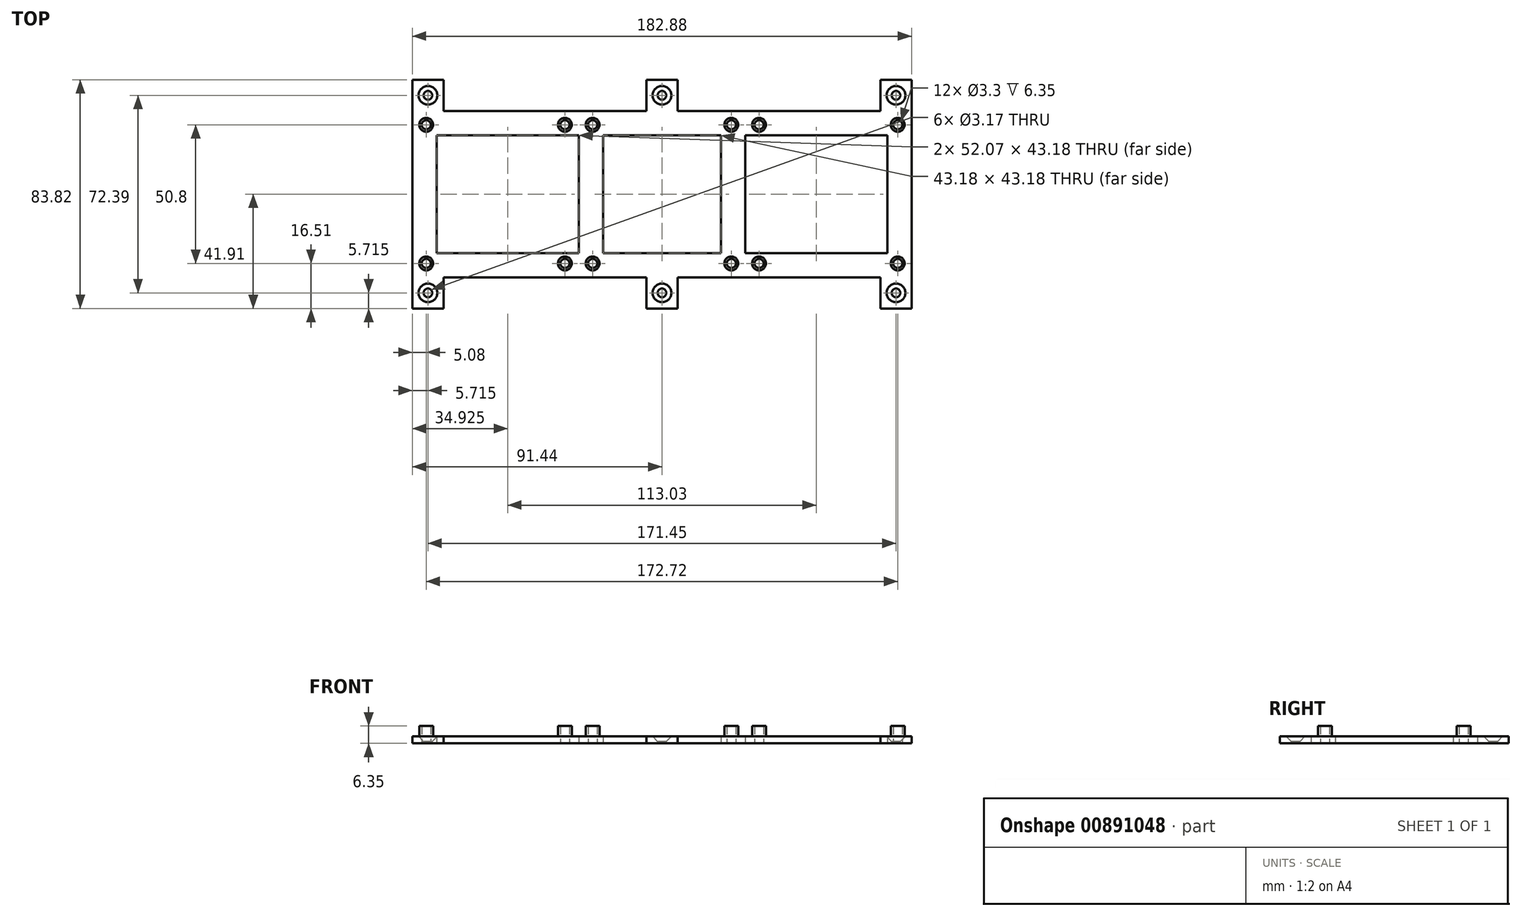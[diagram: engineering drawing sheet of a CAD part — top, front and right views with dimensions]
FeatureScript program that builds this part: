
annotation { "Feature Type Name" : "Feature", "Feature Type Description" : "" }
export const myFeature = defineFeature(function(context is Context, id is Id, definition is map)
    precondition{}
    {
        {
            var Q0;
            Q0=qCreatedBy(makeId("Top.planeOp"),FACE);
            var sketch = newSketch(context, id + "F0", { "sketchPlane" : qUnion([Q0])});
            skLineSegment(sketch, "E0.bottom", {"start": v(30.48, 30.48) * mm, "end": v(-30.48, 30.48) * mm});
            skLineSegment(sketch, "E0.top", {"start": v(30.48, -30.48) * mm, "end": v(-30.48, -30.48) * mm});
            skLineSegment(sketch, "E0.left", {"start": v(30.48, 30.48) * mm, "end": v(30.48, -30.48) * mm});
            skLineSegment(sketch, "E0.right", {"start": v(-30.48, 30.48) * mm, "end": v(-30.48, -30.48) * mm});
            skPoint(sketch, "E0.middle", {"position": v(0, 0) * mm});
            skCircle(sketch, "E1", {"center": v(-25.4, 25.4) * mm, "radius": 2.54 * mm});
            skCircle(sketch, "E2", {"center": v(25.4, 25.4) * mm, "radius": 2.54 * mm});
            skCircle(sketch, "E3", {"center": v(25.4, -25.4) * mm, "radius": 2.54 * mm});
            skCircle(sketch, "E4", {"center": v(-25.4, -25.4) * mm, "radius": 2.54 * mm});
            skLineSegment(sketch, "E5.bottom", {"start": v(21.59, 21.6) * mm, "end": v(-21.59, 21.6) * mm});
            skLineSegment(sketch, "E5.top", {"start": v(21.59, -21.6) * mm, "end": v(-21.59, -21.6) * mm});
            skLineSegment(sketch, "E5.left", {"start": v(21.59, 21.6) * mm, "end": v(21.59, -21.6) * mm});
            skLineSegment(sketch, "E5.right", {"start": v(-21.59, 21.6) * mm, "end": v(-21.59, -21.6) * mm});
            skLineSegment(sketch, "E6.bottom", {"start": v(-30.48, 30.48) * mm, "end": v(-91.44, 30.48) * mm});
            skLineSegment(sketch, "E6.top", {"start": v(-30.48, 21.6) * mm, "end": v(-91.44, 21.6) * mm});
            skLineSegment(sketch, "E6.left", {"start": v(-30.48, 30.48) * mm, "end": v(-30.48, 21.6) * mm});
            skLineSegment(sketch, "E6.right", {"start": v(-91.44, 30.48) * mm, "end": v(-91.44, 21.59) * mm});
            skLineSegment(sketch, "E7.bottom", {"start": v(-30.48, -30.48) * mm, "end": v(-91.44, -30.48) * mm});
            skLineSegment(sketch, "E7.top", {"start": v(-30.48, -21.6) * mm, "end": v(-91.44, -21.6) * mm});
            skLineSegment(sketch, "E7.left", {"start": v(-30.48, -30.48) * mm, "end": v(-30.48, -21.6) * mm});
            skLineSegment(sketch, "E7.right", {"start": v(-91.44, -30.48) * mm, "end": v(-91.44, -21.6) * mm});
            skLineSegment(sketch, "E8.bottom", {"start": v(-91.44, 21.6) * mm, "end": v(-82.55, 21.6) * mm});
            skLineSegment(sketch, "E8.top", {"start": v(-91.44, -21.6) * mm, "end": v(-82.55, -21.6) * mm});
            skLineSegment(sketch, "E8.left", {"start": v(-91.44, 21.59) * mm, "end": v(-91.44, -21.6) * mm});
            skLineSegment(sketch, "E8.right", {"start": v(-82.55, 21.59) * mm, "end": v(-82.55, -21.6) * mm});
            skLineSegment(sketch, "E9.bottom", {"start": v(30.48, 30.48) * mm, "end": v(91.44, 30.48) * mm});
            skLineSegment(sketch, "E9.top", {"start": v(30.48, 21.6) * mm, "end": v(91.44, 21.6) * mm});
            skLineSegment(sketch, "E9.left", {"start": v(30.48, 30.48) * mm, "end": v(30.48, 21.6) * mm});
            skLineSegment(sketch, "E9.right", {"start": v(91.44, 30.48) * mm, "end": v(91.44, 21.6) * mm});
            skLineSegment(sketch, "E10.bottom", {"start": v(30.48, -30.48) * mm, "end": v(91.44, -30.48) * mm});
            skLineSegment(sketch, "E10.top", {"start": v(30.48, -21.6) * mm, "end": v(91.44, -21.6) * mm});
            skLineSegment(sketch, "E10.left", {"start": v(30.48, -30.48) * mm, "end": v(30.48, -21.6) * mm});
            skLineSegment(sketch, "E10.right", {"start": v(91.44, -30.48) * mm, "end": v(91.44, -21.6) * mm});
            skLineSegment(sketch, "E11.bottom", {"start": v(91.44, 21.6) * mm, "end": v(82.55, 21.6) * mm});
            skLineSegment(sketch, "E11.top", {"start": v(91.44, -21.6) * mm, "end": v(82.55, -21.6) * mm});
            skLineSegment(sketch, "E11.left", {"start": v(91.44, 21.6) * mm, "end": v(91.44, -21.6) * mm});
            skLineSegment(sketch, "E11.right", {"start": v(82.55, 21.6) * mm, "end": v(82.55, -21.6) * mm});
            skCircle(sketch, "E12", {"center": v(35.56, 25.4) * mm, "radius": 2.54 * mm});
            skCircle(sketch, "E13", {"center": v(86.36, 25.4) * mm, "radius": 2.54 * mm});
            skCircle(sketch, "E14", {"center": v(86.36, -25.4) * mm, "radius": 2.54 * mm});
            skCircle(sketch, "E15", {"center": v(35.56, -25.4) * mm, "radius": 2.54 * mm});
            skCircle(sketch, "E16", {"center": v(-35.56, 25.4) * mm, "radius": 2.54 * mm});
            skCircle(sketch, "E17", {"center": v(-86.36, 25.4) * mm, "radius": 2.54 * mm});
            skCircle(sketch, "E18", {"center": v(-86.36, -25.4) * mm, "radius": 2.54 * mm});
            skCircle(sketch, "E19", {"center": v(-35.56, -25.4) * mm, "radius": 2.54 * mm});
            skLineSegment(sketch, "E20.bottom", {"start": v(-91.44, 30.48) * mm, "end": v(-80.01, 30.48) * mm});
            skLineSegment(sketch, "E20.top", {"start": v(-91.44, 41.91) * mm, "end": v(-80.01, 41.91) * mm});
            skLineSegment(sketch, "E20.left", {"start": v(-91.44, 30.48) * mm, "end": v(-91.44, 41.91) * mm});
            skLineSegment(sketch, "E20.right", {"start": v(-80.01, 30.48) * mm, "end": v(-80.01, 41.91) * mm});
            skLineSegment(sketch, "E21.bottom", {"start": v(-91.44, -30.48) * mm, "end": v(-80.01, -30.48) * mm});
            skLineSegment(sketch, "E21.top", {"start": v(-91.44, -41.91) * mm, "end": v(-80.01, -41.91) * mm});
            skLineSegment(sketch, "E21.left", {"start": v(-91.44, -30.48) * mm, "end": v(-91.44, -41.91) * mm});
            skLineSegment(sketch, "E21.right", {"start": v(-80.01, -30.48) * mm, "end": v(-80.01, -41.91) * mm});
            skLineSegment(sketch, "E22.bottom", {"start": v(91.44, -30.48) * mm, "end": v(80.01, -30.48) * mm});
            skLineSegment(sketch, "E22.top", {"start": v(91.44, -41.91) * mm, "end": v(80.01, -41.91) * mm});
            skLineSegment(sketch, "E22.left", {"start": v(91.44, -30.48) * mm, "end": v(91.44, -41.91) * mm});
            skLineSegment(sketch, "E22.right", {"start": v(80.01, -30.48) * mm, "end": v(80.01, -41.91) * mm});
            skLineSegment(sketch, "E23.bottom", {"start": v(91.44, 30.48) * mm, "end": v(80.01, 30.48) * mm});
            skLineSegment(sketch, "E23.top", {"start": v(91.44, 41.91) * mm, "end": v(80.01, 41.91) * mm});
            skLineSegment(sketch, "E23.left", {"start": v(91.44, 30.48) * mm, "end": v(91.44, 41.91) * mm});
            skLineSegment(sketch, "E23.right", {"start": v(80.01, 30.48) * mm, "end": v(80.01, 41.91) * mm});
            skLineSegment(sketch, "E24.bottom", {"start": v(-5.72, 30.48) * mm, "end": v(5.71, 30.48) * mm});
            skLineSegment(sketch, "E24.top", {"start": v(-5.72, 41.91) * mm, "end": v(5.71, 41.91) * mm});
            skLineSegment(sketch, "E24.left", {"start": v(-5.72, 30.48) * mm, "end": v(-5.72, 41.91) * mm});
            skLineSegment(sketch, "E24.right", {"start": v(5.71, 30.48) * mm, "end": v(5.71, 41.91) * mm});
            skPoint(sketch, "E25.firstSnap0", {"position": v(-5.72, 36.2) * mm});
            skLineSegment(sketch, "E25.bottom", {"start": v(-5.72, -30.48) * mm, "end": v(5.71, -30.48) * mm});
            skLineSegment(sketch, "E25.top", {"start": v(-5.72, -41.91) * mm, "end": v(5.71, -41.91) * mm});
            skLineSegment(sketch, "E25.left", {"start": v(-5.72, -30.48) * mm, "end": v(-5.72, -41.91) * mm});
            skLineSegment(sketch, "E25.right", {"start": v(5.71, -30.48) * mm, "end": v(5.71, -41.91) * mm});
            skSolve(sketch);
        }
        {
            var Q0;
            Q0=makeQuery(id+"F0.imprint","IMPRINT",FACE,{"disambiguationData":[TD([[makeQuery(id+"F0.imprint","IMPRINT",EDGE,{"derivedFrom":sQuery(id+"F0.wireOp",EDGE,"E1")}),-1.0]])]});
            var Q1;
            {var subQ4=sQuery(id+"F0.wireOp",EDGE,"E6.right");Q1=makeQuery(id+"F0.imprint","IMPRINT",FACE,{"disambiguationData":[TD([[makeQuery(id+"F0.imprint","IMPRINT",EDGE,{"derivedFrom":subQ4}),1.0]])]});}
            var Q2;
            {var subQ0=sQuery(id+"F0.wireOp",EDGE,"E8.left");Q2=makeQuery(id+"F0.imprint","IMPRINT",FACE,{"disambiguationData":[TD([[makeQuery(id+"F0.imprint","IMPRINT",EDGE,{"derivedFrom":subQ0}),1.0]])]});}
            var Q3;
            {var subQ7=sQuery(id+"F0.wireOp",EDGE,"E7.right");Q3=makeQuery(id+"F0.imprint","IMPRINT",FACE,{"disambiguationData":[TD([[makeQuery(id+"F0.imprint","IMPRINT",EDGE,{"derivedFrom":subQ7}),-1.0]])]});}
            var Q4;
            {var subQ4=sQuery(id+"F0.wireOp",EDGE,"E9.right");Q4=makeQuery(id+"F0.imprint","IMPRINT",FACE,{"disambiguationData":[TD([[makeQuery(id+"F0.imprint","IMPRINT",EDGE,{"derivedFrom":subQ4}),-1.0]])]});}
            var Q5;
            {var subQ7=sQuery(id+"F0.wireOp",EDGE,"E10.right");Q5=makeQuery(id+"F0.imprint","IMPRINT",FACE,{"disambiguationData":[TD([[makeQuery(id+"F0.imprint","IMPRINT",EDGE,{"derivedFrom":subQ7}),1.0]])]});}
            var Q6;
            {var subQ0=sQuery(id+"F0.wireOp",EDGE,"E11.left");Q6=makeQuery(id+"F0.imprint","IMPRINT",FACE,{"disambiguationData":[TD([[makeQuery(id+"F0.imprint","IMPRINT",EDGE,{"derivedFrom":subQ0}),-1.0]])]});}
            var Q7;
            Q7=makeQuery(id+"F0.imprint","IMPRINT",FACE,{"disambiguationData":[TD([[makeQuery(id+"F0.imprint","IMPRINT",EDGE,{"derivedFrom":sQuery(id+"F0.wireOp",EDGE,"E20.top")}),-1.0]])]});
            var Q8;
            Q8=makeQuery(id+"F0.imprint","IMPRINT",FACE,{"disambiguationData":[TD([[makeQuery(id+"F0.imprint","IMPRINT",EDGE,{"derivedFrom":sQuery(id+"F0.wireOp",EDGE,"E23.top")}),1.0]])]});
            var Q9;
            Q9=makeQuery(id+"F0.imprint","IMPRINT",FACE,{"disambiguationData":[TD([[makeQuery(id+"F0.imprint","IMPRINT",EDGE,{"derivedFrom":sQuery(id+"F0.wireOp",EDGE,"E22.top")}),-1.0]])]});
            var Q10;
            Q10=makeQuery(id+"F0.imprint","IMPRINT",FACE,{"disambiguationData":[TD([[makeQuery(id+"F0.imprint","IMPRINT",EDGE,{"derivedFrom":sQuery(id+"F0.wireOp",EDGE,"E21.top")}),1.0]])]});
            var Q11;
            Q11=makeQuery(id+"F0.imprint","IMPRINT",FACE,{"disambiguationData":[TD([[makeQuery(id+"F0.imprint","IMPRINT",EDGE,{"derivedFrom":sQuery(id+"F0.wireOp",EDGE,"E24.top")}),-1.0]])]});
            var Q12;
            Q12=makeQuery(id+"F0.imprint","IMPRINT",FACE,{"disambiguationData":[TD([[makeQuery(id+"F0.imprint","IMPRINT",EDGE,{"derivedFrom":sQuery(id+"F0.wireOp",EDGE,"E25.top")}),1.0]])]});
            extrude(context, id + "F1", {"entities" : qUnion([Q0, Q1, Q2, Q3, Q4, Q5, Q6, Q7, Q8, Q9, Q10, Q11, Q12]), "depth" : 2.54 * mm, "offsetDistance" : 25.4 * mm});
        }
        {
            var Q0;
            Q0=makeQuery(id+"F0.imprint","IMPRINT",FACE,{"disambiguationData":[TD([[makeQuery(id+"F0.imprint","IMPRINT",EDGE,{"derivedFrom":sQuery(id+"F0.wireOp",EDGE,"E1")}),1.0]])]});
            var Q1;
            Q1=makeQuery(id+"F0.imprint","IMPRINT",FACE,{"disambiguationData":[TD([[makeQuery(id+"F0.imprint","IMPRINT",EDGE,{"derivedFrom":sQuery(id+"F0.wireOp",EDGE,"E2")}),1.0]])]});
            var Q2;
            Q2=makeQuery(id+"F0.imprint","IMPRINT",FACE,{"disambiguationData":[TD([[makeQuery(id+"F0.imprint","IMPRINT",EDGE,{"derivedFrom":sQuery(id+"F0.wireOp",EDGE,"E3")}),1.0]])]});
            var Q3;
            Q3=makeQuery(id+"F0.imprint","IMPRINT",FACE,{"disambiguationData":[TD([[makeQuery(id+"F0.imprint","IMPRINT",EDGE,{"derivedFrom":sQuery(id+"F0.wireOp",EDGE,"E4")}),1.0]])]});
            var Q4;
            Q4=makeQuery(id+"F0.imprint","IMPRINT",FACE,{"disambiguationData":[TD([[makeQuery(id+"F0.imprint","IMPRINT",EDGE,{"derivedFrom":sQuery(id+"F0.wireOp",EDGE,"E17")}),1.0]])]});
            var Q5;
            Q5=makeQuery(id+"F0.imprint","IMPRINT",FACE,{"disambiguationData":[TD([[makeQuery(id+"F0.imprint","IMPRINT",EDGE,{"derivedFrom":sQuery(id+"F0.wireOp",EDGE,"E18")}),1.0]])]});
            var Q6;
            Q6=makeQuery(id+"F0.imprint","IMPRINT",FACE,{"disambiguationData":[TD([[makeQuery(id+"F0.imprint","IMPRINT",EDGE,{"derivedFrom":sQuery(id+"F0.wireOp",EDGE,"E16")}),1.0]])]});
            var Q7;
            Q7=makeQuery(id+"F0.imprint","IMPRINT",FACE,{"disambiguationData":[TD([[makeQuery(id+"F0.imprint","IMPRINT",EDGE,{"derivedFrom":sQuery(id+"F0.wireOp",EDGE,"E19")}),1.0]])]});
            var Q8;
            Q8=makeQuery(id+"F0.imprint","IMPRINT",FACE,{"disambiguationData":[TD([[makeQuery(id+"F0.imprint","IMPRINT",EDGE,{"derivedFrom":sQuery(id+"F0.wireOp",EDGE,"E15")}),1.0]])]});
            var Q9;
            Q9=makeQuery(id+"F0.imprint","IMPRINT",FACE,{"disambiguationData":[TD([[makeQuery(id+"F0.imprint","IMPRINT",EDGE,{"derivedFrom":sQuery(id+"F0.wireOp",EDGE,"E14")}),1.0]])]});
            var Q10;
            Q10=makeQuery(id+"F0.imprint","IMPRINT",FACE,{"disambiguationData":[TD([[makeQuery(id+"F0.imprint","IMPRINT",EDGE,{"derivedFrom":sQuery(id+"F0.wireOp",EDGE,"E13")}),1.0]])]});
            var Q11;
            Q11=makeQuery(id+"F0.imprint","IMPRINT",FACE,{"disambiguationData":[TD([[makeQuery(id+"F0.imprint","IMPRINT",EDGE,{"derivedFrom":sQuery(id+"F0.wireOp",EDGE,"E12")}),1.0]])]});
            extrude(context, id + "F2", {"entities" : qUnion([Q0, Q1, Q2, Q3, Q4, Q5, Q6, Q7, Q8, Q9, Q10, Q11]), "operationType" : NewBodyOperationType.ADD, "depth" : 6.35 * mm, "offsetDistance" : 25.4 * mm});
        }
        {
            var Q0;
            Q0=sQuery(id+"F0.wireOp",VERTEX,"E1.center");
            var Q1;
            Q1=sQuery(id+"F0.wireOp",VERTEX,"E2.center");
            var Q2;
            Q2=sQuery(id+"F0.wireOp",VERTEX,"E3.center");
            var Q3;
            Q3=sQuery(id+"F0.wireOp",VERTEX,"E4.center");
            var Q4;
            Q4=sQuery(id+"F0.wireOp",VERTEX,"E17.center");
            var Q5;
            Q5=sQuery(id+"F0.wireOp",VERTEX,"E16.center");
            var Q6;
            Q6=sQuery(id+"F0.wireOp",VERTEX,"E18.center");
            var Q7;
            Q7=sQuery(id+"F0.wireOp",VERTEX,"E19.center");
            var Q8;
            Q8=sQuery(id+"F0.wireOp",VERTEX,"E12.center");
            var Q9;
            Q9=sQuery(id+"F0.wireOp",VERTEX,"E13.center");
            var Q10;
            Q10=sQuery(id+"F0.wireOp",VERTEX,"E15.center");
            var Q11;
            Q11=sQuery(id+"F0.wireOp",VERTEX,"E14.center");
            var Q12;
            Q12=makeQuery(id+"F1.opExtrude","SWEPT_BODY",BODY,{"disambiguationData":[OSD([sQuery(id+"F0.wireOp",EDGE,"E0.bottom"),sQuery(id+"F0.wireOp",EDGE,"E0.top"),sQuery(id+"F0.wireOp",EDGE,"E0.left"),sQuery(id+"F0.wireOp",EDGE,"E0.right"),sQuery(id+"F0.wireOp",EDGE,"E1"),sQuery(id+"F0.wireOp",EDGE,"E2"),sQuery(id+"F0.wireOp",EDGE,"E3"),sQuery(id+"F0.wireOp",EDGE,"E4"),sQuery(id+"F0.wireOp",EDGE,"E5.bottom"),sQuery(id+"F0.wireOp",EDGE,"E5.top"),sQuery(id+"F0.wireOp",EDGE,"E5.left"),sQuery(id+"F0.wireOp",EDGE,"E5.right"),sQuery(id+"F0.wireOp",EDGE,"E6.bottom"),sQuery(id+"F0.wireOp",EDGE,"E6.top"),sQuery(id+"F0.wireOp",EDGE,"E6.right"),sQuery(id+"F0.wireOp",EDGE,"E7.bottom"),sQuery(id+"F0.wireOp",EDGE,"E7.top"),sQuery(id+"F0.wireOp",EDGE,"E7.right"),sQuery(id+"F0.wireOp",EDGE,"E8.left"),sQuery(id+"F0.wireOp",EDGE,"E8.right"),sQuery(id+"F0.wireOp",EDGE,"E9.bottom"),sQuery(id+"F0.wireOp",EDGE,"E9.top"),sQuery(id+"F0.wireOp",EDGE,"E9.right"),sQuery(id+"F0.wireOp",EDGE,"E10.bottom"),sQuery(id+"F0.wireOp",EDGE,"E10.top"),sQuery(id+"F0.wireOp",EDGE,"E10.right"),sQuery(id+"F0.wireOp",EDGE,"E11.left"),sQuery(id+"F0.wireOp",EDGE,"E11.right"),sQuery(id+"F0.wireOp",EDGE,"E12"),sQuery(id+"F0.wireOp",EDGE,"E13"),sQuery(id+"F0.wireOp",EDGE,"E14"),sQuery(id+"F0.wireOp",EDGE,"E15"),sQuery(id+"F0.wireOp",EDGE,"E16"),sQuery(id+"F0.wireOp",EDGE,"E17"),sQuery(id+"F0.wireOp",EDGE,"E18"),sQuery(id+"F0.wireOp",EDGE,"E19"),sQuery(id+"F0.wireOp",EDGE,"E20.top"),sQuery(id+"F0.wireOp",EDGE,"E20.left"),sQuery(id+"F0.wireOp",EDGE,"E20.right"),sQuery(id+"F0.wireOp",EDGE,"E21.top"),sQuery(id+"F0.wireOp",EDGE,"E21.left"),sQuery(id+"F0.wireOp",EDGE,"E21.right"),sQuery(id+"F0.wireOp",EDGE,"E22.top"),sQuery(id+"F0.wireOp",EDGE,"E22.left"),sQuery(id+"F0.wireOp",EDGE,"E22.right"),sQuery(id+"F0.wireOp",EDGE,"E23.top"),sQuery(id+"F0.wireOp",EDGE,"E23.left"),sQuery(id+"F0.wireOp",EDGE,"E23.right"),sQuery(id+"F0.wireOp",EDGE,"E24.top"),sQuery(id+"F0.wireOp",EDGE,"E24.left"),sQuery(id+"F0.wireOp",EDGE,"E24.right"),sQuery(id+"F0.wireOp",EDGE,"E25.top"),sQuery(id+"F0.wireOp",EDGE,"E25.left"),sQuery(id+"F0.wireOp",EDGE,"E25.right")])]});
            hole(context, id + "F3", {"style" : HoleStyle.SIMPLE, "endStyle" : HoleEndStyle.THROUGH, "oppositeDirection" : true, "holeDiameter" : 3.3 * mm, "majorDiameter" : 6.35 * mm, "isTappedThrough" : true, "tappedDepth" : 12.7 * mm, "tapClearance" : 3, "locations" : qUnion([Q0, Q1, Q2, Q3, Q4, Q5, Q6, Q7, Q8, Q9, Q10, Q11]), "scope" : qUnion([Q12])});
        }
        {
            var Q0;
            Q0=makeQuery(id+"F1.opExtrude","CAP_FACE",FACE,{"disambiguationData":[OSD([sQuery(id+"F0.wireOp",EDGE,"E0.bottom"),sQuery(id+"F0.wireOp",EDGE,"E0.top"),sQuery(id+"F0.wireOp",EDGE,"E0.left"),sQuery(id+"F0.wireOp",EDGE,"E0.right"),sQuery(id+"F0.wireOp",EDGE,"E1"),sQuery(id+"F0.wireOp",EDGE,"E2"),sQuery(id+"F0.wireOp",EDGE,"E3"),sQuery(id+"F0.wireOp",EDGE,"E4"),sQuery(id+"F0.wireOp",EDGE,"E5.bottom"),sQuery(id+"F0.wireOp",EDGE,"E5.top"),sQuery(id+"F0.wireOp",EDGE,"E5.left"),sQuery(id+"F0.wireOp",EDGE,"E5.right"),sQuery(id+"F0.wireOp",EDGE,"E6.bottom"),sQuery(id+"F0.wireOp",EDGE,"E6.top"),sQuery(id+"F0.wireOp",EDGE,"E6.right"),sQuery(id+"F0.wireOp",EDGE,"E7.bottom"),sQuery(id+"F0.wireOp",EDGE,"E7.top"),sQuery(id+"F0.wireOp",EDGE,"E7.right"),sQuery(id+"F0.wireOp",EDGE,"E8.left"),sQuery(id+"F0.wireOp",EDGE,"E8.right"),sQuery(id+"F0.wireOp",EDGE,"E9.bottom"),sQuery(id+"F0.wireOp",EDGE,"E9.top"),sQuery(id+"F0.wireOp",EDGE,"E9.right"),sQuery(id+"F0.wireOp",EDGE,"E10.bottom"),sQuery(id+"F0.wireOp",EDGE,"E10.top"),sQuery(id+"F0.wireOp",EDGE,"E10.right"),sQuery(id+"F0.wireOp",EDGE,"E11.left"),sQuery(id+"F0.wireOp",EDGE,"E11.right"),sQuery(id+"F0.wireOp",EDGE,"E12"),sQuery(id+"F0.wireOp",EDGE,"E13"),sQuery(id+"F0.wireOp",EDGE,"E14"),sQuery(id+"F0.wireOp",EDGE,"E15"),sQuery(id+"F0.wireOp",EDGE,"E16"),sQuery(id+"F0.wireOp",EDGE,"E17"),sQuery(id+"F0.wireOp",EDGE,"E18"),sQuery(id+"F0.wireOp",EDGE,"E19"),sQuery(id+"F0.wireOp",EDGE,"E20.top"),sQuery(id+"F0.wireOp",EDGE,"E20.left"),sQuery(id+"F0.wireOp",EDGE,"E20.right"),sQuery(id+"F0.wireOp",EDGE,"E21.top"),sQuery(id+"F0.wireOp",EDGE,"E21.left"),sQuery(id+"F0.wireOp",EDGE,"E21.right"),sQuery(id+"F0.wireOp",EDGE,"E22.top"),sQuery(id+"F0.wireOp",EDGE,"E22.left"),sQuery(id+"F0.wireOp",EDGE,"E22.right"),sQuery(id+"F0.wireOp",EDGE,"E23.top"),sQuery(id+"F0.wireOp",EDGE,"E23.left"),sQuery(id+"F0.wireOp",EDGE,"E23.right"),sQuery(id+"F0.wireOp",EDGE,"E24.top"),sQuery(id+"F0.wireOp",EDGE,"E24.left"),sQuery(id+"F0.wireOp",EDGE,"E24.right"),sQuery(id+"F0.wireOp",EDGE,"E25.top"),sQuery(id+"F0.wireOp",EDGE,"E25.left"),sQuery(id+"F0.wireOp",EDGE,"E25.right")])],"isStart":false});
            var sketch = newSketch(context, id + "F4", { "sketchPlane" : qUnion([Q0])});
            skPoint(sketch, "E26", {"position": v(-85.73, 36.2) * mm});
            skPoint(sketch, "E26.positionSnap0", {"position": v(-80.01, 36.2) * mm});
            skPoint(sketch, "E26.positionSnap1", {"position": v(-85.73, 41.91) * mm});
            skPoint(sketch, "E27", {"position": v(85.73, 36.2) * mm});
            skPoint(sketch, "E27.positionSnap0", {"position": v(80.01, 36.2) * mm});
            skPoint(sketch, "E27.positionSnap1", {"position": v(85.73, 41.91) * mm});
            skPoint(sketch, "E28", {"position": v(85.73, -36.2) * mm});
            skPoint(sketch, "E28.positionSnap0", {"position": v(85.73, -41.91) * mm});
            skPoint(sketch, "E28.positionSnap1", {"position": v(80.01, -36.2) * mm});
            skPoint(sketch, "E29", {"position": v(-85.73, -36.2) * mm});
            skPoint(sketch, "E29.positionSnap0", {"position": v(-85.73, -41.91) * mm});
            skPoint(sketch, "E29.positionSnap1", {"position": v(-80.01, -36.2) * mm});
            skPoint(sketch, "E30", {"position": v(0, 36.2) * mm});
            skPoint(sketch, "E30.positionSnap0", {"position": v(5.71, 36.2) * mm});
            skPoint(sketch, "E31", {"position": v(0, -36.2) * mm});
            skPoint(sketch, "E31.positionSnap0", {"position": v(5.71, -36.2) * mm});
            skSolve(sketch);
        }
        {
            var Q0;
            Q0=sQuery(id+"F4.wireOp",VERTEX,"E26");
            var Q1;
            Q1=sQuery(id+"F4.wireOp",VERTEX,"E29");
            var Q2;
            Q2=sQuery(id+"F4.wireOp",VERTEX,"E28");
            var Q3;
            Q3=sQuery(id+"F4.wireOp",VERTEX,"E27");
            var Q4;
            Q4=sQuery(id+"F4.wireOp",VERTEX,"E30");
            var Q5;
            Q5=sQuery(id+"F4.wireOp",VERTEX,"E31");
            var Q6;
            Q6=makeQuery(id+"F1.opExtrude","SWEPT_BODY",BODY,{"disambiguationData":[OSD([sQuery(id+"F0.wireOp",EDGE,"E0.bottom"),sQuery(id+"F0.wireOp",EDGE,"E0.top"),sQuery(id+"F0.wireOp",EDGE,"E0.left"),sQuery(id+"F0.wireOp",EDGE,"E0.right"),sQuery(id+"F0.wireOp",EDGE,"E1"),sQuery(id+"F0.wireOp",EDGE,"E2"),sQuery(id+"F0.wireOp",EDGE,"E3"),sQuery(id+"F0.wireOp",EDGE,"E4"),sQuery(id+"F0.wireOp",EDGE,"E5.bottom"),sQuery(id+"F0.wireOp",EDGE,"E5.top"),sQuery(id+"F0.wireOp",EDGE,"E5.left"),sQuery(id+"F0.wireOp",EDGE,"E5.right"),sQuery(id+"F0.wireOp",EDGE,"E6.bottom"),sQuery(id+"F0.wireOp",EDGE,"E6.top"),sQuery(id+"F0.wireOp",EDGE,"E6.right"),sQuery(id+"F0.wireOp",EDGE,"E7.bottom"),sQuery(id+"F0.wireOp",EDGE,"E7.top"),sQuery(id+"F0.wireOp",EDGE,"E7.right"),sQuery(id+"F0.wireOp",EDGE,"E8.left"),sQuery(id+"F0.wireOp",EDGE,"E8.right"),sQuery(id+"F0.wireOp",EDGE,"E9.bottom"),sQuery(id+"F0.wireOp",EDGE,"E9.top"),sQuery(id+"F0.wireOp",EDGE,"E9.right"),sQuery(id+"F0.wireOp",EDGE,"E10.bottom"),sQuery(id+"F0.wireOp",EDGE,"E10.top"),sQuery(id+"F0.wireOp",EDGE,"E10.right"),sQuery(id+"F0.wireOp",EDGE,"E11.left"),sQuery(id+"F0.wireOp",EDGE,"E11.right"),sQuery(id+"F0.wireOp",EDGE,"E12"),sQuery(id+"F0.wireOp",EDGE,"E13"),sQuery(id+"F0.wireOp",EDGE,"E14"),sQuery(id+"F0.wireOp",EDGE,"E15"),sQuery(id+"F0.wireOp",EDGE,"E16"),sQuery(id+"F0.wireOp",EDGE,"E17"),sQuery(id+"F0.wireOp",EDGE,"E18"),sQuery(id+"F0.wireOp",EDGE,"E19"),sQuery(id+"F0.wireOp",EDGE,"E20.top"),sQuery(id+"F0.wireOp",EDGE,"E20.left"),sQuery(id+"F0.wireOp",EDGE,"E20.right"),sQuery(id+"F0.wireOp",EDGE,"E21.top"),sQuery(id+"F0.wireOp",EDGE,"E21.left"),sQuery(id+"F0.wireOp",EDGE,"E21.right"),sQuery(id+"F0.wireOp",EDGE,"E22.top"),sQuery(id+"F0.wireOp",EDGE,"E22.left"),sQuery(id+"F0.wireOp",EDGE,"E22.right"),sQuery(id+"F0.wireOp",EDGE,"E23.top"),sQuery(id+"F0.wireOp",EDGE,"E23.left"),sQuery(id+"F0.wireOp",EDGE,"E23.right"),sQuery(id+"F0.wireOp",EDGE,"E24.top"),sQuery(id+"F0.wireOp",EDGE,"E24.left"),sQuery(id+"F0.wireOp",EDGE,"E24.right"),sQuery(id+"F0.wireOp",EDGE,"E25.top"),sQuery(id+"F0.wireOp",EDGE,"E25.left"),sQuery(id+"F0.wireOp",EDGE,"E25.right")])]});
            hole(context, id + "F5", {"style" : HoleStyle.C_SINK, "endStyle" : HoleEndStyle.THROUGH, "holeDiameter" : 3.17 * mm, "cSinkDiameter" : 6.86 * mm, "cSinkAngle" : 90 * degree, "majorDiameter" : 6.35 * mm, "isTappedThrough" : true, "tappedDepth" : 12.7 * mm, "tapClearance" : 3, "locations" : qUnion([Q0, Q1, Q2, Q3, Q4, Q5]), "scope" : qUnion([Q6])});
        }
    });
